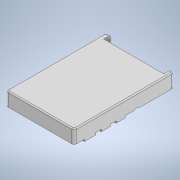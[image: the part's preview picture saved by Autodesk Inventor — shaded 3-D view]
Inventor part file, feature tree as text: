
AUTODESK INVENTOR PART (.ipt)
format: ipt  version: 2020 (Build 240168000, 168)  size: 215,040 bytes
history: native  units: mm
features: extrude x7, sketch x6, fillet x1
ambient origin geometry x8: Origin, YZ Plane, XZ Plane, XY Plane, X Axis, Y Axis, Z Axis, Center Point
bodies: Solid1 (feature_tree)
feature tree (14):
  sketch  "Sketch1"  dims[d2=60.0mm d3=88.0mm]
  extrude  "Extrusion1"  Depth=88.0mm
  extrude  "Extrusion2"  Depth=56.0mm
  extrude  "Extrusion3"  Depth=2.0mm
  sketch  "Sketch3"  dims[d6=3.0mm d7=2.0mm]
  extrude  "Extrusion4"  Depth=8.0mm TaperAngle=0.0deg
  extrude  "Extrusion5"  Depth=4.0mm
  extrude  "Extrusion6"  Depth=19.0mm TaperAngle=0.0deg
  sketch  "Sketch5"  dims[d12=4.0mm d13=4.0mm]
  extrude  "Extrusion7"  Depth=16.0mm
  fillet  "Fillet1"  Radius=2.5mm
  sketch  "Sketch2"  dims[d4=56.0mm d5=85.0mm]
  sketch  "Sketch4"  dims[d8=4.0mm d9=0.0mm d10=8.0mm d11=0.0mm]
  sketch  "Sketch6"  dims[d14=11.0mm d15=19.0mm d16=0.0mm d17=16.0mm d18=2.5mm d19=21.0mm d20=0.0mm d21=5.0mm d22=0.0mm d27=2.5mm d28=32.5mm d29=7.0mm d30=10.0mm d31=0.0mm d32=1.7mm d33=10.5mm d34=8.0mm d35=5.0mm d36=8.0mm d37=5.0mm d38=10.0mm d39=1.7mm d40=2.0mm d41=0.0mm d42=1.0mm d43=0.872665mm]
